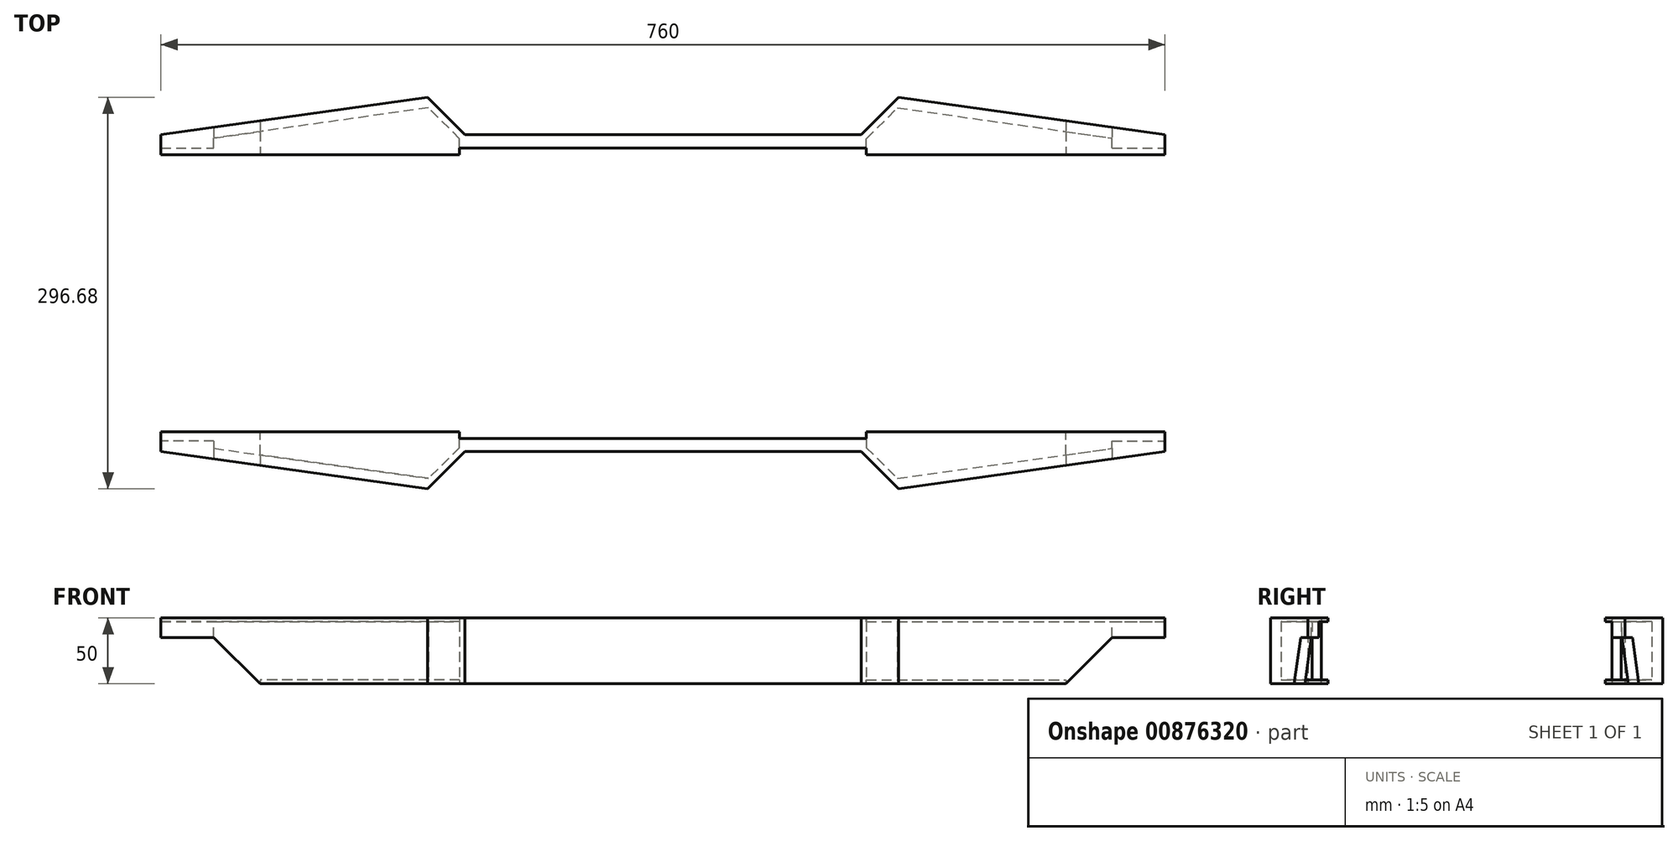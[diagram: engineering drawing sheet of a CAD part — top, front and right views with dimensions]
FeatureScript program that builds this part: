
annotation { "Feature Type Name" : "Feature", "Feature Type Description" : "" }
export const myFeature = defineFeature(function(context is Context, id is Id, definition is map)
    precondition{}
    {
        {
            var Q0;
            Q0=qCreatedBy(makeId("Top.planeOp"),FACE);
            var sketch = newSketch(context, id + "F0", { "sketchPlane" : qUnion([Q0])});
            skLineSegment(sketch, "E0", {"start": v(-380, 120) * mm, "end": v(-380, -120) * mm});
            skLineSegment(sketch, "E1", {"start": v(380, 120) * mm, "end": v(380, -120) * mm});
            skLineSegment(sketch, "E2", {"start": v(150, -120) * mm, "end": v(-150, -120) * mm});
            skLineSegment(sketch, "E3", {"start": v(-150, 120) * mm, "end": v(150, 120) * mm});
            skLineSegment(sketch, "E4", {"start": v(-160, 110) * mm, "end": v(160, 110) * mm, "construction": true});
            skLineSegment(sketch, "E5", {"start": v(160, 110) * mm, "end": v(160, -110) * mm, "construction": true});
            skLineSegment(sketch, "E6", {"start": v(160, -110) * mm, "end": v(-160, -110) * mm, "construction": true});
            skLineSegment(sketch, "E7", {"start": v(-160, -110) * mm, "end": v(-160, 110) * mm, "construction": true});
            skLineSegment(sketch, "E8.0", {"start": v(-150, -110) * mm, "end": v(-150, 110) * mm, "construction": true});
            skLineSegment(sketch, "E9.0", {"start": v(150, 110) * mm, "end": v(150, -110) * mm, "construction": true});
            skLineSegment(sketch, "E10", {"start": v(-150, -110) * mm, "end": v(-150, -120) * mm, "construction": true});
            skLineSegment(sketch, "E11", {"start": v(-150, 110) * mm, "end": v(-150, 120) * mm, "construction": true});
            skLineSegment(sketch, "E12", {"start": v(-150, 120) * mm, "end": v(-178.34, 148.34) * mm});
            skLineSegment(sketch, "E13", {"start": v(-380, 120) * mm, "end": v(-178.34, 148.34) * mm});
            skPoint(sketch, "E14.endSnap0", {"position": v(0, 110) * mm});
            skLineSegment(sketch, "E15.MirrorCS", {"start": v(150, 120) * mm, "end": v(178.34, 148.34) * mm});
            skLineSegment(sketch, "E16.MirrorCS", {"start": v(380, 120) * mm, "end": v(178.34, 148.34) * mm});
            skLineSegment(sketch, "E17.MirrorCS", {"start": v(-150, -120) * mm, "end": v(-178.34, -148.34) * mm, "construction": true});
            skLineSegment(sketch, "E18.MirrorCS", {"start": v(-380, -120) * mm, "end": v(-178.34, -148.34) * mm});
            skLineSegment(sketch, "E19.MirrorCS", {"start": v(150, -120) * mm, "end": v(178.34, -148.34) * mm});
            skLineSegment(sketch, "E20.MirrorCS", {"start": v(-150, -120) * mm, "end": v(-178.34, -148.34) * mm});
            skLineSegment(sketch, "E21.MirrorCS", {"start": v(380, -120) * mm, "end": v(178.34, -148.34) * mm});
            skSolve(sketch);
        }
        {
            var Q0;
            Q0=makeQuery(id+"F0.imprint","IMPRINT",FACE,{"disambiguationData":[TD([[makeQuery(id+"F0.imprint","IMPRINT",EDGE,{"derivedFrom":sQuery(id+"F0.wireOp",EDGE,"E0")}),1.0]])]});
            extrude(context, id + "F1", {"entities" : qUnion([Q0]), "depth" : 50 * mm, "offsetDistance" : 25 * mm});
        }
        {
            var Q0;
            Q0=makeQuery(id+"F1.opExtrude","SWEPT_FACE",FACE,{"disambiguationData":[OSD([sQuery(id+"F0.wireOp",EDGE,"E2")])]});
            var sketch = newSketch(context, id + "F2", { "sketchPlane" : qUnion([Q0])});
            skLineSegment(sketch, "E22", {"start": v(-380, 35) * mm, "end": v(-340, 35) * mm});
            skLineSegment(sketch, "E23", {"start": v(-340, 35) * mm, "end": v(-305, 0) * mm});
            skLineSegment(sketch, "E24", {"start": v(-380, 35) * mm, "end": v(-380, 0) * mm});
            skLineSegment(sketch, "E25", {"start": v(-380, 0) * mm, "end": v(-305, 0) * mm});
            skLineSegment(sketch, "E26.MirrorCS", {"start": v(380, 0) * mm, "end": v(305, 0) * mm});
            skLineSegment(sketch, "E27.MirrorCS", {"start": v(380, 35) * mm, "end": v(380, 0) * mm});
            skLineSegment(sketch, "E28.MirrorCS", {"start": v(380, 35) * mm, "end": v(340, 35) * mm});
            skLineSegment(sketch, "E29.MirrorCS", {"start": v(340, 35) * mm, "end": v(305, 0) * mm});
            skSolve(sketch);
        }
        {
            var Q0;
            Q0=makeQuery(id+"F1.opExtrude","SWEPT_FACE",FACE,{"disambiguationData":[OSD([sQuery(id+"F0.wireOp",EDGE,"E0")])]});
            var sketch = newSketch(context, id + "F3", { "sketchPlane" : qUnion([Q0])});
            skLineSegment(sketch, "E30.0", {"start": v(-110, 45) * mm, "end": v(110, 45) * mm});
            skLineSegment(sketch, "E31.0", {"start": v(-110, 5) * mm, "end": v(110, 5) * mm});
            skLineSegment(sketch, "E32.0", {"start": v(-110, 5) * mm, "end": v(-110, 45) * mm});
            skLineSegment(sketch, "E33.0", {"start": v(110, 45) * mm, "end": v(110, 5) * mm});
            skSolve(sketch);
        }
        {
            var Q0;
            Q0=makeQuery(id+"F3.imprint","IMPRINT",FACE,{"disambiguationData":[TD([[makeQuery(id+"F3.imprint","IMPRINT",EDGE,{"derivedFrom":sQuery(id+"F3.wireOp",EDGE,"E30.0")}),-1.0]])]});
            extrude(context, id + "F4", {"entities" : qUnion([Q0]), "operationType" : NewBodyOperationType.REMOVE, "oppositeDirection" : true, "depth" : 760 * mm, "offsetDistance" : 25 * mm});
        }
        {
            var Q0;
            Q0=makeQuery(id+"F2.imprint","IMPRINT",FACE,{"disambiguationData":[TD([[makeQuery(id+"F2.imprint","IMPRINT",EDGE,{"derivedFrom":sQuery(id+"F2.wireOp",EDGE,"E26.MirrorCS")}),-1.0]])]});
            var Q1;
            Q1=makeQuery(id+"F2.imprint","IMPRINT",FACE,{"disambiguationData":[TD([[makeQuery(id+"F2.imprint","IMPRINT",EDGE,{"derivedFrom":sQuery(id+"F2.wireOp",EDGE,"E22")}),-1.0]])]});
            extrude(context, id + "F5", {"entities" : qUnion([Q0, Q1]), "operationType" : NewBodyOperationType.REMOVE, "oppositeDirection" : true, "depth" : 240 * mm, "offsetDistance" : 25 * mm});
        }
        {
            var Q0;
            Q0=makeQuery(id+"F1.opExtrude","CAP_FACE",FACE,{"disambiguationData":[OSD([sQuery(id+"F0.wireOp",EDGE,"E0"),sQuery(id+"F0.wireOp",EDGE,"E1"),sQuery(id+"F0.wireOp",EDGE,"E2"),sQuery(id+"F0.wireOp",EDGE,"E3")])],"isStart":false});
            var sketch = newSketch(context, id + "F6", { "sketchPlane" : qUnion([Q0])});
            skLineSegment(sketch, "E34", {"start": v(-140, 90) * mm, "end": v(140, 90) * mm});
            skLineSegment(sketch, "E35", {"start": v(140, 90) * mm, "end": v(140, -90) * mm});
            skLineSegment(sketch, "E36", {"start": v(140, -90) * mm, "end": v(-140, -90) * mm});
            skLineSegment(sketch, "E37", {"start": v(-140, -90) * mm, "end": v(-140, 90) * mm});
            skLineSegment(sketch, "E38", {"start": v(160, 110) * mm, "end": v(160, -110) * mm});
            skLineSegment(sketch, "E39", {"start": v(-160, 110) * mm, "end": v(-160, -110) * mm});
            skLineSegment(sketch, "E40", {"start": v(-160, 110) * mm, "end": v(160, 110) * mm});
            skLineSegment(sketch, "E41", {"start": v(160, -110) * mm, "end": v(-160, -110) * mm});
            skSolve(sketch);
        }
        {
            var Q0;
            Q0=qSketchRegion(id+"F6",true);
            extrude(context, id + "F7", {"entities" : qUnion([Q0]), "operationType" : NewBodyOperationType.REMOVE, "oppositeDirection" : true, "depth" : 50 * mm, "offsetDistance" : 25 * mm});
        }
        {
            var Q0;
            Q0=qSketchRegion(id+"F2",true);
            extrude(context, id + "F8", {"entities" : qUnion([Q0]), "operationType" : NewBodyOperationType.REMOVE, "endBound" : BoundingType.SYMMETRIC, "oppositeDirection" : true, "depth" : 871.86 * mm, "offsetDistance" : 25 * mm});
        }
        {
            var Q0;
            {var subQ0=sQuery(id+"F0.wireOp",EDGE,"E18.MirrorCS");var subQ1=sQuery(id+"F0.wireOp",EDGE,"E16.MirrorCS");var subQ2=sQuery(id+"F0.wireOp",EDGE,"E15.MirrorCS");var subQ3=sQuery(id+"F0.wireOp",EDGE,"E13");var subQ4=sQuery(id+"F0.wireOp",EDGE,"E12");var subQ5=sQuery(id+"F0.wireOp",EDGE,"E19.MirrorCS");var subQ6=sQuery(id+"F0.wireOp",EDGE,"E0");var subQ7=sQuery(id+"F0.wireOp",EDGE,"E3");var subQ8=sQuery(id+"F0.wireOp",EDGE,"E1");var subQ9=sQuery(id+"F0.wireOp",EDGE,"E2");var subQ10=sQuery(id+"F0.wireOp",EDGE,"E20.MirrorCS");var subQ11=sQuery(id+"F0.wireOp",EDGE,"E21.MirrorCS");Q0=makeQuery(id+"F7.boolean.opBoolean","SPLIT",FACE,{"disambiguationData":[TD([makeQuery(id+"F1.opExtrude","SWEPT_FACE",FACE,{"disambiguationData":[OSD([subQ6])]})])],"derivedFrom":makeQuery(id+"F1.opExtrude","CAP_FACE",FACE,{"disambiguationData":[OSD([subQ6,subQ8,subQ9,subQ7,subQ4,subQ3,subQ2,subQ1,subQ0,subQ5,subQ10,subQ11])],"isStart":false})});}
            var sketch = newSketch(context, id + "F9", { "sketchPlane" : qUnion([Q0])});
            skLineSegment(sketch, "E42", {"start": v(-165, -110) * mm, "end": v(-305, -110) * mm});
            skLineSegment(sketch, "E43", {"start": v(-305, -110) * mm, "end": v(-305, 110) * mm});
            skLineSegment(sketch, "E44", {"start": v(-305, 110) * mm, "end": v(-165, 110) * mm});
            skLineSegment(sketch, "E45.0", {"start": v(-165, 110) * mm, "end": v(-165, -110) * mm});
            skLineSegment(sketch, "E46", {"start": v(0, 0) * mm, "end": v(0, 58.76) * mm});
            skLineSegment(sketch, "E47.MirrorCS", {"start": v(165, 110) * mm, "end": v(165, -110) * mm});
            skLineSegment(sketch, "E48.MirrorCS", {"start": v(165, -110) * mm, "end": v(305, -110) * mm});
            skLineSegment(sketch, "E49.MirrorCS", {"start": v(305, -110) * mm, "end": v(305, 110) * mm});
            skLineSegment(sketch, "E50.MirrorCS", {"start": v(305, 110) * mm, "end": v(165, 110) * mm});
            skSolve(sketch);
        }
        {
            var Q0;
            Q0=makeQuery(id+"F9.imprint","IMPRINT",FACE,{"disambiguationData":[TD([[makeQuery(id+"F9.imprint","IMPRINT",EDGE,{"derivedFrom":sQuery(id+"F9.wireOp",EDGE,"E42")}),-1.0]])]});
            var Q1;
            Q1=makeQuery(id+"F9.imprint","IMPRINT",FACE,{"disambiguationData":[TD([[makeQuery(id+"F9.imprint","IMPRINT",EDGE,{"derivedFrom":sQuery(id+"F9.wireOp",EDGE,"E47.MirrorCS")}),1.0]])]});
            extrude(context, id + "F10", {"entities" : qUnion([Q0, Q1]), "operationType" : NewBodyOperationType.REMOVE, "oppositeDirection" : true, "depth" : 10 * mm, "offsetDistance" : 25 * mm});
        }
        {
            var Q0;
            Q0=makeQuery(id+"F1.opExtrude","SWEPT_FACE",FACE,{"disambiguationData":[OSD([sQuery(id+"F0.wireOp",EDGE,"E2")])]});
            var sketch = newSketch(context, id + "F11", { "sketchPlane" : qUnion([Q0])});
            skLineSegment(sketch, "E51", {"start": v(-305, 50) * mm, "end": v(-305, 0) * mm});
            skLineSegment(sketch, "E52", {"start": v(-340, 50) * mm, "end": v(-340, 35) * mm});
            skLineSegment(sketch, "E53", {"start": v(-340, 35) * mm, "end": v(-305, 0) * mm});
            skLineSegment(sketch, "E54.0", {"start": v(-332.93, 35) * mm, "end": v(-305, 7.07) * mm});
            skLineSegment(sketch, "E55", {"start": v(-340, 35) * mm, "end": v(-332.93, 35) * mm});
            skLineSegment(sketch, "E56", {"start": v(0, 0) * mm, "end": v(0, 50) * mm});
            skLineSegment(sketch, "E57", {"start": v(-340, 35) * mm, "end": v(-346.55, 35) * mm});
            skLineSegment(sketch, "E58.MirrorCS", {"start": v(332.93, 35) * mm, "end": v(305, 7.07) * mm});
            skLineSegment(sketch, "E59.MirrorCS", {"start": v(340, 35) * mm, "end": v(305, 0) * mm});
            skLineSegment(sketch, "E60.MirrorCS", {"start": v(340, 35) * mm, "end": v(332.93, 35) * mm});
            skLineSegment(sketch, "E61", {"start": v(305, 7.07) * mm, "end": v(305, 0) * mm});
            skSolve(sketch);
        }
        {
            var Q0;
            {var subQ0=sQuery(id+"F11.wireOp",EDGE,"E53");Q0=makeQuery(id+"F11.imprint","IMPRINT",FACE,{"disambiguationData":[TD([[makeQuery(id+"F11.imprint","IMPRINT",EDGE,{"derivedFrom":subQ0}),1.0]])]});}
            var Q1;
            Q1=makeQuery(id+"F11.imprint","IMPRINT",FACE,{"disambiguationData":[TD([[makeQuery(id+"F11.imprint","IMPRINT",EDGE,{"derivedFrom":sQuery(id+"F11.wireOp",EDGE,"E58.MirrorCS")}),1.0]])]});
            extrude(context, id + "F12", {"entities" : qUnion([Q0, Q1]), "oppositeDirection" : true, "depth" : 240 * mm, "offsetDistance" : 25 * mm});
        }
        {
            var Q0;
            Q0=makeQuery(id+"F7.boolean.opBoolean","SPLIT",FACE,{"disambiguationData":[TD([makeQuery(id+"F7.opExtrude","SWEPT_FACE",FACE,{"disambiguationData":[OSD([sQuery(id+"F6.wireOp",EDGE,"E34")])]})])],"derivedFrom":makeQuery(id+"F1.opExtrude","CAP_FACE",FACE,{"disambiguationData":[OSD([sQuery(id+"F0.wireOp",EDGE,"E0"),sQuery(id+"F0.wireOp",EDGE,"E1"),sQuery(id+"F0.wireOp",EDGE,"E2"),sQuery(id+"F0.wireOp",EDGE,"E3"),sQuery(id+"F0.wireOp",EDGE,"E12"),sQuery(id+"F0.wireOp",EDGE,"E13"),sQuery(id+"F0.wireOp",EDGE,"E15.MirrorCS"),sQuery(id+"F0.wireOp",EDGE,"E16.MirrorCS"),sQuery(id+"F0.wireOp",EDGE,"E18.MirrorCS"),sQuery(id+"F0.wireOp",EDGE,"E19.MirrorCS"),sQuery(id+"F0.wireOp",EDGE,"E20.MirrorCS"),sQuery(id+"F0.wireOp",EDGE,"E21.MirrorCS")])],"isStart":false})});
            extrude(context, id + "F13", {"entities" : qUnion([Q0]), "operationType" : NewBodyOperationType.REMOVE, "oppositeDirection" : true, "depth" : 25 * mm, "offsetDistance" : 25 * mm});
        }
        {
            var Q0;
            Q0=makeQuery(id+"F7.boolean.opBoolean","SPLIT",FACE,{"disambiguationData":[TD([makeQuery(id+"F7.opExtrude","SWEPT_FACE",FACE,{"disambiguationData":[OSD([sQuery(id+"F6.wireOp",EDGE,"E34")])]})])],"derivedFrom":makeQuery(id+"F1.opExtrude","CAP_FACE",FACE,{"disambiguationData":[OSD([sQuery(id+"F0.wireOp",EDGE,"E0"),sQuery(id+"F0.wireOp",EDGE,"E1"),sQuery(id+"F0.wireOp",EDGE,"E2"),sQuery(id+"F0.wireOp",EDGE,"E3"),sQuery(id+"F0.wireOp",EDGE,"E12"),sQuery(id+"F0.wireOp",EDGE,"E13"),sQuery(id+"F0.wireOp",EDGE,"E15.MirrorCS"),sQuery(id+"F0.wireOp",EDGE,"E16.MirrorCS"),sQuery(id+"F0.wireOp",EDGE,"E18.MirrorCS"),sQuery(id+"F0.wireOp",EDGE,"E19.MirrorCS"),sQuery(id+"F0.wireOp",EDGE,"E20.MirrorCS"),sQuery(id+"F0.wireOp",EDGE,"E21.MirrorCS")])],"isStart":true})});
            extrude(context, id + "F14", {"entities" : qUnion([Q0]), "operationType" : NewBodyOperationType.REMOVE, "oppositeDirection" : true, "depth" : 25 * mm, "offsetDistance" : 25 * mm});
        }
        {
            var Q0;
            Q0=makeQuery(id+"F7.boolean.opBoolean","COPY",FACE,{"disambiguationData":[TD([makeQuery(id+"F4.boolean.opBoolean","COPY",FACE,{"derivedFrom":makeQuery(id+"F4.opExtrude","SWEPT_FACE",FACE,{"disambiguationData":[OSD([sQuery(id+"F3.wireOp",EDGE,"E30.0")])]})})])],"derivedFrom":makeQuery(id+"F7.opExtrude","SWEPT_FACE",FACE,{"disambiguationData":[OSD([sQuery(id+"F6.wireOp",EDGE,"E38")])]})});
            var sketch = newSketch(context, id + "F15", { "sketchPlane" : qUnion([Q0])});
            skLineSegment(sketch, "E62", {"start": v(-110, 45) * mm, "end": v(-110, 5) * mm});
            skLineSegment(sketch, "E63", {"start": v(-110, 45) * mm, "end": v(110, 45) * mm});
            skLineSegment(sketch, "E64", {"start": v(110, 45) * mm, "end": v(110, 5) * mm});
            skLineSegment(sketch, "E65", {"start": v(-110, 5) * mm, "end": v(110, 5) * mm});
            skSolve(sketch);
        }
        {
            var Q0;
            Q0=makeQuery(id+"F7.boolean.opBoolean","COPY",FACE,{"disambiguationData":[TD([makeQuery(id+"F4.boolean.opBoolean","COPY",FACE,{"derivedFrom":makeQuery(id+"F4.opExtrude","SWEPT_FACE",FACE,{"disambiguationData":[OSD([sQuery(id+"F3.wireOp",EDGE,"E31.0")])]})})])],"derivedFrom":makeQuery(id+"F7.opExtrude","SWEPT_FACE",FACE,{"disambiguationData":[OSD([sQuery(id+"F6.wireOp",EDGE,"E39")])]})});
            var sketch = newSketch(context, id + "F16", { "sketchPlane" : qUnion([Q0])});
            skLineSegment(sketch, "E66", {"start": v(-110, 5) * mm, "end": v(-110, 45) * mm});
            skLineSegment(sketch, "E67", {"start": v(-110, 5) * mm, "end": v(110, 5) * mm});
            skLineSegment(sketch, "E68", {"start": v(110, 5) * mm, "end": v(110, 45) * mm});
            skLineSegment(sketch, "E69", {"start": v(-110, 45) * mm, "end": v(110, 45) * mm});
            skSolve(sketch);
        }
        {
            var Q0;
            Q0=qSketchRegion(id+"F16",true);
            extrude(context, id + "F17", {"entities" : qUnion([Q0]), "operationType" : NewBodyOperationType.ADD, "oppositeDirection" : true, "depth" : 5 * mm, "offsetDistance" : 25 * mm});
        }
        {
            var Q0;
            Q0=makeQuery(id+"F15.imprint","IMPRINT",FACE,{"disambiguationData":[TD([[makeQuery(id+"F15.imprint","IMPRINT",EDGE,{"derivedFrom":sQuery(id+"F15.wireOp",EDGE,"E62")}),1.0]])]});
            extrude(context, id + "F18", {"entities" : qUnion([Q0]), "operationType" : NewBodyOperationType.ADD, "oppositeDirection" : true, "depth" : 5 * mm, "offsetDistance" : 25 * mm});
        }
        {
            var Q0;
            Q0=makeQuery(id+"F7.boolean.opBoolean","SPLIT",BODY,{"disambiguationData":[OD(0.0)],"derivedFrom":makeQuery(id+"F1.opExtrude","SWEPT_BODY",BODY,{"disambiguationData":[OSD([sQuery(id+"F0.wireOp",EDGE,"E0"),sQuery(id+"F0.wireOp",EDGE,"E1"),sQuery(id+"F0.wireOp",EDGE,"E2"),sQuery(id+"F0.wireOp",EDGE,"E3"),sQuery(id+"F0.wireOp",EDGE,"E12"),sQuery(id+"F0.wireOp",EDGE,"E13"),sQuery(id+"F0.wireOp",EDGE,"E15.MirrorCS"),sQuery(id+"F0.wireOp",EDGE,"E16.MirrorCS"),sQuery(id+"F0.wireOp",EDGE,"E18.MirrorCS"),sQuery(id+"F0.wireOp",EDGE,"E19.MirrorCS"),sQuery(id+"F0.wireOp",EDGE,"E20.MirrorCS"),sQuery(id+"F0.wireOp",EDGE,"E21.MirrorCS")])]})});
            var Q1;
            Q1=makeQuery(id+"F12.opExtrude","SWEPT_BODY",BODY,{"disambiguationData":[OSD([sQuery(id+"F11.wireOp",EDGE,"E51"),sQuery(id+"F11.wireOp",EDGE,"E53"),sQuery(id+"F11.wireOp",EDGE,"E54.0"),sQuery(id+"F11.wireOp",EDGE,"E55")])]});
            var Q2;
            Q2=makeQuery(id+"F12.opExtrude","SWEPT_BODY",BODY,{"disambiguationData":[OSD([sQuery(id+"F11.wireOp",EDGE,"E58.MirrorCS"),sQuery(id+"F11.wireOp",EDGE,"E59.MirrorCS"),sQuery(id+"F11.wireOp",EDGE,"E60.MirrorCS"),sQuery(id+"F11.wireOp",EDGE,"E61")])]});
            booleanBodies(context, id + "F19", {"operationType" : BooleanOperationType.UNION, "tools" : qUnion([Q0, Q1, Q2])});
        }
        {
            var Q0;
            Q0=makeQuery(id+"F10.boolean.opBoolean","COPY",FACE,{"derivedFrom":makeQuery(id+"F10.opExtrude","SWEPT_FACE",FACE,{"disambiguationData":[OSD([sQuery(id+"F9.wireOp",EDGE,"E43")])]})});
            extrude(context, id + "F20", {"entities" : qUnion([Q0]), "operationType" : NewBodyOperationType.REMOVE, "oppositeDirection" : true, "depth" : 121.6 * mm, "offsetDistance" : 25 * mm});
        }
        {
            var Q0;
            Q0=makeQuery(id+"F10.boolean.opBoolean","COPY",FACE,{"derivedFrom":makeQuery(id+"F10.opExtrude","SWEPT_FACE",FACE,{"disambiguationData":[OSD([sQuery(id+"F9.wireOp",EDGE,"E49.MirrorCS")])]})});
            extrude(context, id + "F21", {"entities" : qUnion([Q0]), "operationType" : NewBodyOperationType.REMOVE, "endBound" : BoundingType.SYMMETRIC, "depth" : 2865.48 * mm, "offsetDistance" : 25 * mm});
        }
        {
            var Q0;
            Q0=makeQuery(id+"F17.boolean.opBoolean","MERGE",FACE,{"derivedFrom":[makeQuery(id+"F10.boolean.opBoolean","COPY",FACE,{"derivedFrom":makeQuery(id+"F10.opExtrude","SWEPT_FACE",FACE,{"disambiguationData":[OSD([sQuery(id+"F9.wireOp",EDGE,"E45.0")])]})}),makeQuery(id+"F17.opExtrude","CAP_FACE",FACE,{"disambiguationData":[OSD([sQuery(id+"F16.wireOp",EDGE,"E66"),sQuery(id+"F16.wireOp",EDGE,"E67"),sQuery(id+"F16.wireOp",EDGE,"E68"),sQuery(id+"F16.wireOp",EDGE,"E69")])],"isStart":false})]});
            extrude(context, id + "F22", {"entities" : qUnion([Q0]), "operationType" : NewBodyOperationType.REMOVE, "endBound" : BoundingType.SYMMETRIC, "oppositeDirection" : true, "depth" : 1589.2 * mm, "offsetDistance" : 25 * mm});
        }
        {
            var Q0;
            {var subQ16=makeQuery(id+"F7.opExtrude","SWEPT_FACE",FACE,{"disambiguationData":[OSD([sQuery(id+"F6.wireOp",EDGE,"E39")])]});Q0=makeQuery(id+"F17.boolean.opBoolean","MERGE",FACE,{"derivedFrom":[makeQuery(id+"F7.boolean.opBoolean","COPY",FACE,{"disambiguationData":[TD([makeQuery(id+"F4.boolean.opBoolean","COPY",FACE,{"derivedFrom":makeQuery(id+"F4.opExtrude","SWEPT_FACE",FACE,{"disambiguationData":[OSD([sQuery(id+"F3.wireOp",EDGE,"E30.0")])]})})])],"derivedFrom":subQ16}),makeQuery(id+"F7.boolean.opBoolean","COPY",FACE,{"disambiguationData":[TD([makeQuery(id+"F4.boolean.opBoolean","COPY",FACE,{"derivedFrom":makeQuery(id+"F4.opExtrude","SWEPT_FACE",FACE,{"disambiguationData":[OSD([sQuery(id+"F3.wireOp",EDGE,"E31.0")])]})})])],"derivedFrom":subQ16}),makeQuery(id+"F17.opExtrude","CAP_FACE",FACE,{"disambiguationData":[OSD([sQuery(id+"F16.wireOp",EDGE,"E66"),sQuery(id+"F16.wireOp",EDGE,"E67"),sQuery(id+"F16.wireOp",EDGE,"E68"),sQuery(id+"F16.wireOp",EDGE,"E69")])],"isStart":true})]});}
            extrude(context, id + "F23", {"entities" : qUnion([Q0]), "operationType" : NewBodyOperationType.REMOVE, "endBound" : BoundingType.SYMMETRIC, "depth" : 1696.6 * mm, "offsetDistance" : 25 * mm});
        }
        {
            var Q0;
            {var subQ1=sQuery(id+"F0.wireOp",EDGE,"E19.MirrorCS");var subQ3=sQuery(id+"F0.wireOp",EDGE,"E21.MirrorCS");var subQ7=sQuery(id+"F0.wireOp",EDGE,"E2");var subQ8=makeQuery(id+"F1.opExtrude","SWEPT_FACE",FACE,{"disambiguationData":[OSD([subQ7])]});var subQ9=sQuery(id+"F0.wireOp",EDGE,"E18.MirrorCS");var subQ13=sQuery(id+"F0.wireOp",EDGE,"E20.MirrorCS");var subQ17=sQuery(id+"F0.wireOp",EDGE,"E16.MirrorCS");var subQ18=sQuery(id+"F0.wireOp",EDGE,"E15.MirrorCS");var subQ22=sQuery(id+"F0.wireOp",EDGE,"E3");var subQ23=sQuery(id+"F0.wireOp",EDGE,"E12");var subQ27=sQuery(id+"F0.wireOp",EDGE,"E13");Q0=makeQuery(id+"F23.boolean.opBoolean","SPLIT",FACE,{"disambiguationData":[TD([subQ8])],"derivedFrom":makeQuery(id+"F7.boolean.opBoolean","SPLIT",FACE,{"disambiguationData":[TD([subQ8])],"derivedFrom":makeQuery(id+"F1.opExtrude","CAP_FACE",FACE,{"disambiguationData":[OSD([sQuery(id+"F0.wireOp",EDGE,"E0"),sQuery(id+"F0.wireOp",EDGE,"E1"),subQ7,subQ22,subQ23,subQ27,subQ18,subQ17,subQ9,subQ1,subQ13,subQ3])],"isStart":true})})});}
            var sketch = newSketch(context, id + "F24", { "sketchPlane" : qUnion([Q0])});
            skLineSegment(sketch, "E70", {"start": v(-301, 110) * mm, "end": v(-154, 110) * mm});
            skLineSegment(sketch, "E71.0", {"start": v(-177.46, 140.39) * mm, "end": v(-301, 123.02) * mm});
            skLineSegment(sketch, "E72.0", {"start": v(-301, 123.02) * mm, "end": v(-301, 110) * mm});
            skLineSegment(sketch, "E73.0", {"start": v(-154, 116.93) * mm, "end": v(-177.46, 140.39) * mm});
            skLineSegment(sketch, "E74.0", {"start": v(-154, 110) * mm, "end": v(-154, 116.93) * mm});
            skLineSegment(sketch, "E75.MirrorCS", {"start": v(-301, -110) * mm, "end": v(-154, -110) * mm});
            skLineSegment(sketch, "E76.MirrorCS", {"start": v(-177.46, -140.39) * mm, "end": v(-301, -123.02) * mm});
            skLineSegment(sketch, "E77.MirrorCS", {"start": v(-301, -123.02) * mm, "end": v(-301, -110) * mm});
            skLineSegment(sketch, "E78.MirrorCS", {"start": v(-154, -116.93) * mm, "end": v(-177.46, -140.39) * mm});
            skLineSegment(sketch, "E79.MirrorCS", {"start": v(-154, -110) * mm, "end": v(-154, -116.93) * mm});
            skLineSegment(sketch, "E80.MirrorCS", {"start": v(154, 116.93) * mm, "end": v(177.46, 140.39) * mm});
            skLineSegment(sketch, "E81.MirrorCS", {"start": v(301, 110) * mm, "end": v(154, 110) * mm});
            skLineSegment(sketch, "E82.MirrorCS", {"start": v(301, -110) * mm, "end": v(154, -110) * mm});
            skLineSegment(sketch, "E83.MirrorCS", {"start": v(154, 110) * mm, "end": v(154, 116.93) * mm});
            skLineSegment(sketch, "E84.MirrorCS", {"start": v(177.46, 140.39) * mm, "end": v(301, 123.02) * mm});
            skLineSegment(sketch, "E85.MirrorCS", {"start": v(301, 123.02) * mm, "end": v(301, 110) * mm});
            skLineSegment(sketch, "E86.MirrorCS", {"start": v(154, -110) * mm, "end": v(154, -116.93) * mm});
            skLineSegment(sketch, "E87.MirrorCS", {"start": v(154, -116.93) * mm, "end": v(177.46, -140.39) * mm});
            skLineSegment(sketch, "E88.MirrorCS", {"start": v(301, -123.02) * mm, "end": v(301, -110) * mm});
            skLineSegment(sketch, "E89.MirrorCS", {"start": v(177.46, -140.39) * mm, "end": v(301, -123.02) * mm});
            skSolve(sketch);
        }
        {
            var Q0;
            Q0=makeQuery(id+"F24.imprint","IMPRINT",FACE,{"disambiguationData":[TD([[makeQuery(id+"F24.imprint","IMPRINT",EDGE,{"derivedFrom":sQuery(id+"F24.wireOp",EDGE,"E75.MirrorCS")}),-1.0]])]});
            var Q1;
            Q1=makeQuery(id+"F24.imprint","IMPRINT",FACE,{"disambiguationData":[TD([[makeQuery(id+"F24.imprint","IMPRINT",EDGE,{"derivedFrom":sQuery(id+"F24.wireOp",EDGE,"E86.MirrorCS")}),1.0]])]});
            extrude(context, id + "F25", {"entities" : qUnion([Q0, Q1]), "operationType" : NewBodyOperationType.REMOVE, "oppositeDirection" : true, "depth" : 50 * mm, "offsetDistance" : 25 * mm});
        }
        {
            var Q0;
            Q0=makeQuery(id+"F24.imprint","IMPRINT",FACE,{"disambiguationData":[TD([[makeQuery(id+"F24.imprint","IMPRINT",EDGE,{"derivedFrom":sQuery(id+"F24.wireOp",EDGE,"E70")}),-1.0]])]});
            var Q1;
            Q1=makeQuery(id+"F24.imprint","IMPRINT",FACE,{"disambiguationData":[TD([[makeQuery(id+"F24.imprint","IMPRINT",EDGE,{"derivedFrom":sQuery(id+"F24.wireOp",EDGE,"E80.MirrorCS")}),-1.0]])]});
            extrude(context, id + "F26", {"entities" : qUnion([Q0, Q1]), "operationType" : NewBodyOperationType.REMOVE, "oppositeDirection" : true, "depth" : 50 * mm, "offsetDistance" : 25 * mm});
        }
        {
            var Q0;
            {var subQ0=sQuery(id+"F0.wireOp",EDGE,"E2");var subQ1=makeQuery(id+"F1.opExtrude","SWEPT_FACE",FACE,{"disambiguationData":[OSD([subQ0])]});var subQ2=sQuery(id+"F0.wireOp",EDGE,"E1");var subQ4=sQuery(id+"F0.wireOp",EDGE,"E18.MirrorCS");var subQ6=sQuery(id+"F0.wireOp",EDGE,"E0");var subQ7=makeQuery(id+"F1.opExtrude","SWEPT_FACE",FACE,{"disambiguationData":[OSD([subQ6])]});var subQ8=sQuery(id+"F0.wireOp",EDGE,"E19.MirrorCS");var subQ10=sQuery(id+"F0.wireOp",EDGE,"E20.MirrorCS");var subQ12=sQuery(id+"F0.wireOp",EDGE,"E21.MirrorCS");var subQ15=sQuery(id+"F0.wireOp",EDGE,"E16.MirrorCS");var subQ16=sQuery(id+"F0.wireOp",EDGE,"E15.MirrorCS");var subQ17=sQuery(id+"F0.wireOp",EDGE,"E13");var subQ18=sQuery(id+"F0.wireOp",EDGE,"E12");var subQ19=sQuery(id+"F0.wireOp",EDGE,"E3");Q0=makeQuery(id+"F21.boolean.opBoolean","SPLIT",FACE,{"disambiguationData":[TD([subQ1])],"derivedFrom":makeQuery(id+"F7.boolean.opBoolean","SPLIT",FACE,{"disambiguationData":[TD([subQ7])],"derivedFrom":makeQuery(id+"F1.opExtrude","CAP_FACE",FACE,{"disambiguationData":[OSD([subQ6,subQ2,subQ0,subQ19,subQ18,subQ17,subQ16,subQ15,subQ4,subQ8,subQ10,subQ12])],"isStart":false})})});}
            var sketch = newSketch(context, id + "F27", { "sketchPlane" : qUnion([Q0])});
            skLineSegment(sketch, "E90.0", {"start": v(301, -123.02) * mm, "end": v(340, -117.54) * mm});
            skLineSegment(sketch, "E91", {"start": v(340, -110) * mm, "end": v(340, -117.54) * mm});
            skLineSegment(sketch, "E92", {"start": v(301, -110) * mm, "end": v(340, -110) * mm});
            skLineSegment(sketch, "E93", {"start": v(301, -110) * mm, "end": v(301, -123.02) * mm});
            skLineSegment(sketch, "E94.MirrorCS", {"start": v(-301, -110) * mm, "end": v(-301, -123.02) * mm});
            skLineSegment(sketch, "E95.MirrorCS", {"start": v(-301, -110) * mm, "end": v(-340, -110) * mm});
            skLineSegment(sketch, "E96.MirrorCS", {"start": v(-340, -110) * mm, "end": v(-340, -117.54) * mm});
            skLineSegment(sketch, "E97.MirrorCS", {"start": v(-301, -123.02) * mm, "end": v(-340, -117.54) * mm});
            skLineSegment(sketch, "E98.MirrorCS", {"start": v(340, 110) * mm, "end": v(340, 117.54) * mm});
            skLineSegment(sketch, "E99.MirrorCS", {"start": v(301, 110) * mm, "end": v(340, 110) * mm});
            skLineSegment(sketch, "E100.MirrorCS", {"start": v(301, 123.02) * mm, "end": v(340, 117.54) * mm});
            skLineSegment(sketch, "E101.MirrorCS", {"start": v(301, 110) * mm, "end": v(301, 123.02) * mm});
            skLineSegment(sketch, "E102.MirrorCS", {"start": v(-301, 110) * mm, "end": v(-301, 123.02) * mm});
            skLineSegment(sketch, "E103.MirrorCS", {"start": v(-301, 110) * mm, "end": v(-340, 110) * mm});
            skLineSegment(sketch, "E104.MirrorCS", {"start": v(-301, 123.02) * mm, "end": v(-340, 117.54) * mm});
            skLineSegment(sketch, "E105.MirrorCS", {"start": v(-340, 110) * mm, "end": v(-340, 117.54) * mm});
            skSolve(sketch);
        }
        {
            var Q0;
            Q0=qSketchRegion(id+"F27",true);
            extrude(context, id + "F28", {"entities" : qUnion([Q0]), "operationType" : NewBodyOperationType.REMOVE, "oppositeDirection" : true, "depth" : 50 * mm, "offsetDistance" : 25 * mm});
        }
        {
            var Q0;
            Q0=makeQuery(id+"F26.boolean.opBoolean","COPY",FACE,{"derivedFrom":makeQuery(id+"F26.opExtrude","SWEPT_FACE",FACE,{"disambiguationData":[OSD([sQuery(id+"F24.wireOp",EDGE,"E83.MirrorCS")])]})});
            var sketch = newSketch(context, id + "F29", { "sketchPlane" : qUnion([Q0])});
            skLineSegment(sketch, "E106", {"start": v(-110, 47) * mm, "end": v(-110, 3) * mm});
            skLineSegment(sketch, "E107.0", {"start": v(-112, 47) * mm, "end": v(-112, 3) * mm});
            skLineSegment(sketch, "E108.MirrorCS", {"start": v(110, 47) * mm, "end": v(110, 3) * mm});
            skLineSegment(sketch, "E109.MirrorCS", {"start": v(112, 47) * mm, "end": v(112, 3) * mm});
            skLineSegment(sketch, "E110", {"start": v(-110, 3) * mm, "end": v(-112, 3) * mm});
            skLineSegment(sketch, "E111", {"start": v(-110, 47) * mm, "end": v(-112, 47) * mm});
            skLineSegment(sketch, "E112.MirrorCS", {"start": v(110, 3) * mm, "end": v(112, 3) * mm});
            skLineSegment(sketch, "E113.MirrorCS", {"start": v(110, 47) * mm, "end": v(112, 47) * mm});
            skSolve(sketch);
        }
        {
            var Q0;
            Q0=makeQuery(id+"F29.imprint","IMPRINT",FACE,{"disambiguationData":[TD([[makeQuery(id+"F29.imprint","IMPRINT",EDGE,{"derivedFrom":sQuery(id+"F29.wireOp",EDGE,"E106")}),-1.0]])]});
            var Q1;
            Q1=makeQuery(id+"F29.imprint","IMPRINT",FACE,{"disambiguationData":[TD([[makeQuery(id+"F29.imprint","IMPRINT",EDGE,{"derivedFrom":sQuery(id+"F29.wireOp",EDGE,"ca43fbb2-e32b-444a-a71d-7a7fd8a9ca550.MirrorCS")}),1.0]])]});
            extrude(context, id + "F30", {"entities" : qUnion([Q0, Q1]), "operationType" : NewBodyOperationType.REMOVE, "endBound" : BoundingType.SYMMETRIC, "oppositeDirection" : true, "depth" : 1554.04 * mm, "offsetDistance" : 25 * mm});
        }
        {
            var Q0;
            Q0=makeQuery(id+"F29.imprint","IMPRINT",FACE,{"disambiguationData":[TD([[makeQuery(id+"F29.imprint","IMPRINT",EDGE,{"derivedFrom":sQuery(id+"F29.wireOp",EDGE,"E106")}),-1.0]])]});
            var Q1;
            Q1=makeQuery(id+"F29.imprint","IMPRINT",FACE,{"disambiguationData":[TD([[makeQuery(id+"F29.imprint","IMPRINT",EDGE,{"derivedFrom":sQuery(id+"F29.wireOp",EDGE,"ca43fbb2-e32b-444a-a71d-7a7fd8a9ca550.MirrorCS")}),1.0]])]});
            extrude(context, id + "F31", {"entities" : qUnion([Q0, Q1]), "operationType" : NewBodyOperationType.ADD, "oppositeDirection" : true, "depth" : 308 * mm, "offsetDistance" : 25 * mm});
        }
        {
            var Q0;
            {var subQ0=sQuery(id+"F0.wireOp",EDGE,"E12");var subQ2=sQuery(id+"F0.wireOp",EDGE,"E1");var subQ4=sQuery(id+"F0.wireOp",EDGE,"E3");var subQ5=makeQuery(id+"F1.opExtrude","SWEPT_FACE",FACE,{"disambiguationData":[OSD([subQ4])]});var subQ6=sQuery(id+"F0.wireOp",EDGE,"E0");var subQ7=makeQuery(id+"F1.opExtrude","SWEPT_FACE",FACE,{"disambiguationData":[OSD([subQ6])]});var subQ8=sQuery(id+"F0.wireOp",EDGE,"E13");var subQ10=sQuery(id+"F0.wireOp",EDGE,"E15.MirrorCS");var subQ12=sQuery(id+"F0.wireOp",EDGE,"E16.MirrorCS");var subQ15=sQuery(id+"F0.wireOp",EDGE,"E18.MirrorCS");var subQ16=sQuery(id+"F0.wireOp",EDGE,"E19.MirrorCS");var subQ17=sQuery(id+"F0.wireOp",EDGE,"E2");var subQ18=sQuery(id+"F0.wireOp",EDGE,"E20.MirrorCS");var subQ19=sQuery(id+"F0.wireOp",EDGE,"E21.MirrorCS");Q0=makeQuery(id+"F21.boolean.opBoolean","SPLIT",FACE,{"disambiguationData":[TD([subQ5])],"derivedFrom":makeQuery(id+"F7.boolean.opBoolean","SPLIT",FACE,{"disambiguationData":[TD([subQ7])],"derivedFrom":makeQuery(id+"F1.opExtrude","CAP_FACE",FACE,{"disambiguationData":[OSD([subQ6,subQ2,subQ17,subQ4,subQ0,subQ8,subQ10,subQ12,subQ15,subQ16,subQ18,subQ19])],"isStart":false})})});}
            var sketch = newSketch(context, id + "F32", { "sketchPlane" : qUnion([Q0])});
            skLineSegment(sketch, "E114", {"start": v(380, 110) * mm, "end": v(340, 110) * mm});
            skLineSegment(sketch, "E115", {"start": v(250.64, 241.62) * mm, "end": v(250.64, 241.62) * mm});
            skLineSegment(sketch, "E116.trimOffspring", {"start": v(-340, 110) * mm, "end": v(-380, 110) * mm});
            skLineSegment(sketch, "E117", {"start": v(-340, 105) * mm, "end": v(-380, 105) * mm});
            skLineSegment(sketch, "E118", {"start": v(340, 105) * mm, "end": v(380, 105) * mm});
            skLineSegment(sketch, "E119", {"start": v(380, 110) * mm, "end": v(380, 105) * mm});
            skLineSegment(sketch, "E120", {"start": v(-380, 105) * mm, "end": v(-380, 110) * mm});
            skLineSegment(sketch, "E121.MirrorCS", {"start": v(-154, -110) * mm, "end": v(-154, -105) * mm});
            skLineSegment(sketch, "E122.MirrorCS", {"start": v(-380, -105) * mm, "end": v(-380, -110) * mm});
            skLineSegment(sketch, "E123.MirrorCS", {"start": v(-340, -105) * mm, "end": v(-380, -105) * mm});
            skLineSegment(sketch, "E124.MirrorCS", {"start": v(-340, -110) * mm, "end": v(-380, -110) * mm});
            skLineSegment(sketch, "E125.MirrorCS", {"start": v(-340, -110) * mm, "end": v(-340, -105) * mm});
            skLineSegment(sketch, "E126.MirrorCS", {"start": v(154, -105) * mm, "end": v(154, -110) * mm});
            skLineSegment(sketch, "E127.MirrorCS", {"start": v(340, -105) * mm, "end": v(340, -110) * mm});
            skLineSegment(sketch, "E128.MirrorCS", {"start": v(380, -110) * mm, "end": v(380, -105) * mm});
            skLineSegment(sketch, "E129.MirrorCS", {"start": v(340, -105) * mm, "end": v(380, -105) * mm});
            skLineSegment(sketch, "E130.MirrorCS", {"start": v(380, -110) * mm, "end": v(340, -110) * mm});
            skLineSegment(sketch, "E131", {"start": v(-340, 110) * mm, "end": v(-340, 117.54) * mm});
            skLineSegment(sketch, "E132", {"start": v(-340, 117.54) * mm, "end": v(-177.46, 140.39) * mm});
            skLineSegment(sketch, "E133", {"start": v(-177.46, 140.39) * mm, "end": v(-154, 116.93) * mm});
            skLineSegment(sketch, "E134", {"start": v(-154, 116.93) * mm, "end": v(-154, 110) * mm});
            skLineSegment(sketch, "E135", {"start": v(-154, 105) * mm, "end": v(-340, 105) * mm});
            skLineSegment(sketch, "E136", {"start": v(154, 110) * mm, "end": v(154, 116.93) * mm});
            skLineSegment(sketch, "E137", {"start": v(154, 116.93) * mm, "end": v(177.46, 140.39) * mm});
            skLineSegment(sketch, "E138", {"start": v(177.46, 140.39) * mm, "end": v(340, 117.54) * mm});
            skLineSegment(sketch, "E139", {"start": v(340, 117.54) * mm, "end": v(340, 110) * mm});
            skLineSegment(sketch, "E140", {"start": v(340, 105) * mm, "end": v(154, 105) * mm});
            skLineSegment(sketch, "E141.MirrorCS", {"start": v(-154, -105) * mm, "end": v(-340, -105) * mm});
            skLineSegment(sketch, "E142.MirrorCS", {"start": v(-340, -117.54) * mm, "end": v(-177.46, -140.39) * mm});
            skLineSegment(sketch, "E143.MirrorCS", {"start": v(-340, -110) * mm, "end": v(-340, -117.54) * mm});
            skLineSegment(sketch, "E144.MirrorCS", {"start": v(-177.46, -140.39) * mm, "end": v(-154, -116.93) * mm});
            skLineSegment(sketch, "E145.MirrorCS", {"start": v(-154, -116.93) * mm, "end": v(-154, -110) * mm});
            skLineSegment(sketch, "E146.MirrorCS", {"start": v(154, -116.93) * mm, "end": v(177.46, -140.39) * mm});
            skLineSegment(sketch, "E147.MirrorCS", {"start": v(177.46, -140.39) * mm, "end": v(340, -117.54) * mm});
            skLineSegment(sketch, "E148.MirrorCS", {"start": v(154, -110) * mm, "end": v(154, -116.93) * mm});
            skLineSegment(sketch, "E149.MirrorCS", {"start": v(340, -117.54) * mm, "end": v(340, -110) * mm});
            skLineSegment(sketch, "E150.MirrorCS", {"start": v(340, -105) * mm, "end": v(154, -105) * mm});
            skLineSegment(sketch, "E151", {"start": v(-154, 110) * mm, "end": v(-154, 105) * mm});
            skLineSegment(sketch, "E152.MirrorCS", {"start": v(154, -110) * mm, "end": v(154, -105) * mm});
            skLineSegment(sketch, "E153.MirrorCS", {"start": v(154, 110) * mm, "end": v(154, 105) * mm});
            skSolve(sketch);
        }
        {
            var Q0;
            Q0=qSketchRegion(id+"F32",true);
            extrude(context, id + "F33", {"entities" : qUnion([Q0]), "operationType" : NewBodyOperationType.ADD, "oppositeDirection" : true, "depth" : 3 * mm, "offsetDistance" : 25 * mm});
        }
        {
            var Q0;
            {var subQ0=sQuery(id+"F0.wireOp",EDGE,"E16.MirrorCS");var subQ4=sQuery(id+"F0.wireOp",EDGE,"E3");var subQ5=makeQuery(id+"F1.opExtrude","SWEPT_FACE",FACE,{"disambiguationData":[OSD([subQ4])]});var subQ8=sQuery(id+"F0.wireOp",EDGE,"E15.MirrorCS");var subQ11=sQuery(id+"F0.wireOp",EDGE,"E12");var subQ13=sQuery(id+"F0.wireOp",EDGE,"E13");var subQ17=sQuery(id+"F0.wireOp",EDGE,"E21.MirrorCS");var subQ18=sQuery(id+"F0.wireOp",EDGE,"E20.MirrorCS");var subQ19=sQuery(id+"F0.wireOp",EDGE,"E19.MirrorCS");var subQ20=sQuery(id+"F0.wireOp",EDGE,"E18.MirrorCS");var subQ21=sQuery(id+"F0.wireOp",EDGE,"E2");Q0=makeQuery(id+"F23.boolean.opBoolean","SPLIT",FACE,{"disambiguationData":[TD([subQ5])],"derivedFrom":makeQuery(id+"F7.boolean.opBoolean","SPLIT",FACE,{"disambiguationData":[TD([makeQuery(id+"F1.opExtrude","SWEPT_FACE",FACE,{"disambiguationData":[OSD([subQ21])]})])],"derivedFrom":makeQuery(id+"F1.opExtrude","CAP_FACE",FACE,{"disambiguationData":[OSD([sQuery(id+"F0.wireOp",EDGE,"E0"),sQuery(id+"F0.wireOp",EDGE,"E1"),subQ21,subQ4,subQ11,subQ13,subQ8,subQ0,subQ20,subQ19,subQ18,subQ17])],"isStart":true})})});}
            var sketch = newSketch(context, id + "F34", { "sketchPlane" : qUnion([Q0])});
            skLineSegment(sketch, "E154", {"start": v(-154, -110) * mm, "end": v(-154, -116.93) * mm});
            skLineSegment(sketch, "E155", {"start": v(-154, -116.93) * mm, "end": v(-177.46, -140.39) * mm});
            skLineSegment(sketch, "E156", {"start": v(-177.46, -140.39) * mm, "end": v(-305, -122.46) * mm});
            skLineSegment(sketch, "E157", {"start": v(-305, -122.46) * mm, "end": v(-305, -110) * mm});
            skLineSegment(sketch, "E158.0", {"start": v(-154, -105) * mm, "end": v(-305, -105) * mm});
            skLineSegment(sketch, "E159", {"start": v(-305, -110) * mm, "end": v(-305, -105) * mm});
            skLineSegment(sketch, "E160", {"start": v(-154, -105) * mm, "end": v(-154, -110) * mm});
            skLineSegment(sketch, "E161.MirrorCS", {"start": v(-154, 105) * mm, "end": v(-305, 105) * mm});
            skLineSegment(sketch, "E162.MirrorCS", {"start": v(-154, 116.93) * mm, "end": v(-177.46, 140.39) * mm});
            skLineSegment(sketch, "E163.MirrorCS", {"start": v(-177.46, 140.39) * mm, "end": v(-305, 122.46) * mm});
            skLineSegment(sketch, "E164.MirrorCS", {"start": v(-154, 105) * mm, "end": v(-154, 110) * mm});
            skLineSegment(sketch, "E165.MirrorCS", {"start": v(-154, 110) * mm, "end": v(-154, 116.93) * mm});
            skLineSegment(sketch, "E166.MirrorCS", {"start": v(-305, 110) * mm, "end": v(-305, 105) * mm});
            skLineSegment(sketch, "E167.MirrorCS", {"start": v(-305, 122.46) * mm, "end": v(-305, 110) * mm});
            skLineSegment(sketch, "E168.MirrorCS", {"start": v(154, -105) * mm, "end": v(154, -110) * mm});
            skLineSegment(sketch, "E169.MirrorCS", {"start": v(154, -110) * mm, "end": v(154, -116.93) * mm});
            skLineSegment(sketch, "E170.MirrorCS", {"start": v(154, -116.93) * mm, "end": v(177.46, -140.39) * mm});
            skLineSegment(sketch, "E171.MirrorCS", {"start": v(154, -105) * mm, "end": v(305, -105) * mm});
            skLineSegment(sketch, "E172.MirrorCS", {"start": v(305, -122.46) * mm, "end": v(305, -110) * mm});
            skLineSegment(sketch, "E173.MirrorCS", {"start": v(177.46, -140.39) * mm, "end": v(305, -122.46) * mm});
            skLineSegment(sketch, "E174.MirrorCS", {"start": v(305, -110) * mm, "end": v(305, -105) * mm});
            skLineSegment(sketch, "E175.MirrorCS", {"start": v(154, 105) * mm, "end": v(305, 105) * mm});
            skLineSegment(sketch, "E176.MirrorCS", {"start": v(177.46, 140.39) * mm, "end": v(305, 122.46) * mm});
            skLineSegment(sketch, "E177.MirrorCS", {"start": v(305, 122.46) * mm, "end": v(305, 110) * mm});
            skLineSegment(sketch, "E178.MirrorCS", {"start": v(305, 110) * mm, "end": v(305, 105) * mm});
            skLineSegment(sketch, "E179.MirrorCS", {"start": v(154, 105) * mm, "end": v(154, 110) * mm});
            skLineSegment(sketch, "E180.MirrorCS", {"start": v(154, 116.93) * mm, "end": v(177.46, 140.39) * mm});
            skLineSegment(sketch, "E181.MirrorCS", {"start": v(154, 110) * mm, "end": v(154, 116.93) * mm});
            skSolve(sketch);
        }
        {
            var Q0;
            Q0=qSketchRegion(id+"F34",true);
            extrude(context, id + "F35", {"entities" : qUnion([Q0]), "operationType" : NewBodyOperationType.ADD, "oppositeDirection" : true, "depth" : 3 * mm, "offsetDistance" : 25 * mm});
        }
    });
